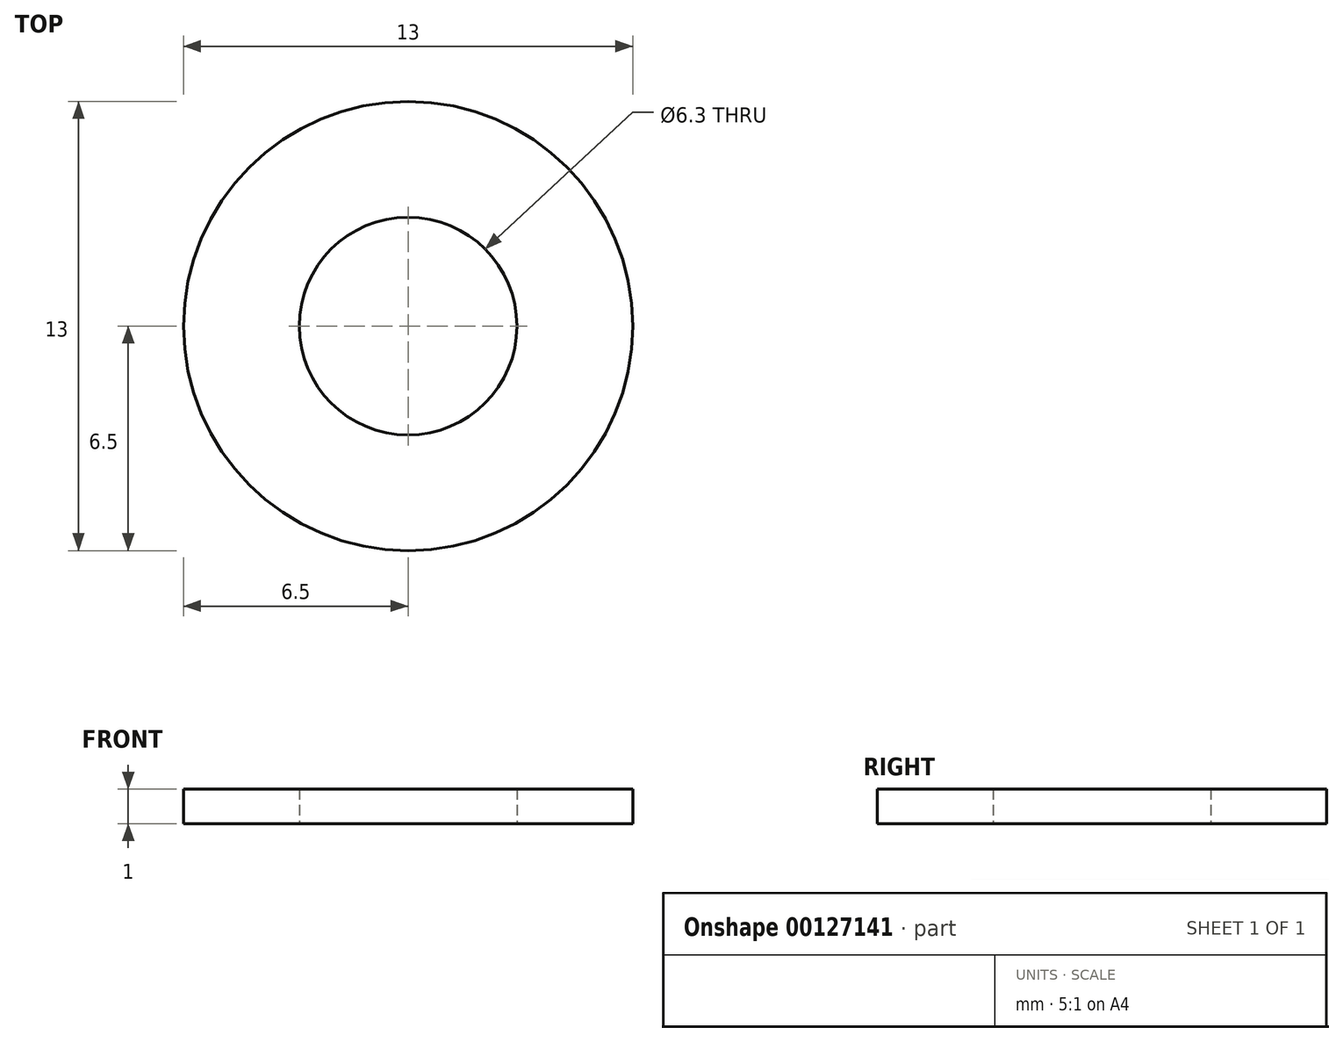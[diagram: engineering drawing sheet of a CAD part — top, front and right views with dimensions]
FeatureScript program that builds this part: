
annotation { "Feature Type Name" : "Feature", "Feature Type Description" : "" }
export const myFeature = defineFeature(function(context is Context, id is Id, definition is map)
    precondition{}
    {
        {
            var Q0;
            Q0=qCreatedBy(makeId("Top.planeOp"),FACE);
            var sketch = newSketch(context, id + "F0", { "sketchPlane" : qUnion([Q0])});
            skCircle(sketch, "E0", {"center": v(0, 0) * mm, "radius": 6.5 * mm});
            skCircle(sketch, "E1", {"center": v(0, 0) * mm, "radius": 3.15 * mm});
            skSolve(sketch);
        }
        {
            var Q0;
            Q0=makeQuery(id+"F0.imprint","IMPRINT",FACE,{"disambiguationData":[TD([[makeQuery(id+"F0.imprint","IMPRINT",EDGE,{"derivedFrom":sQuery(id+"F0.wireOp",EDGE,"E0")}),1.0]])]});
            extrude(context, id + "F1", {"entities" : qUnion([Q0]), "depth" : 1 * mm});
        }
    });
